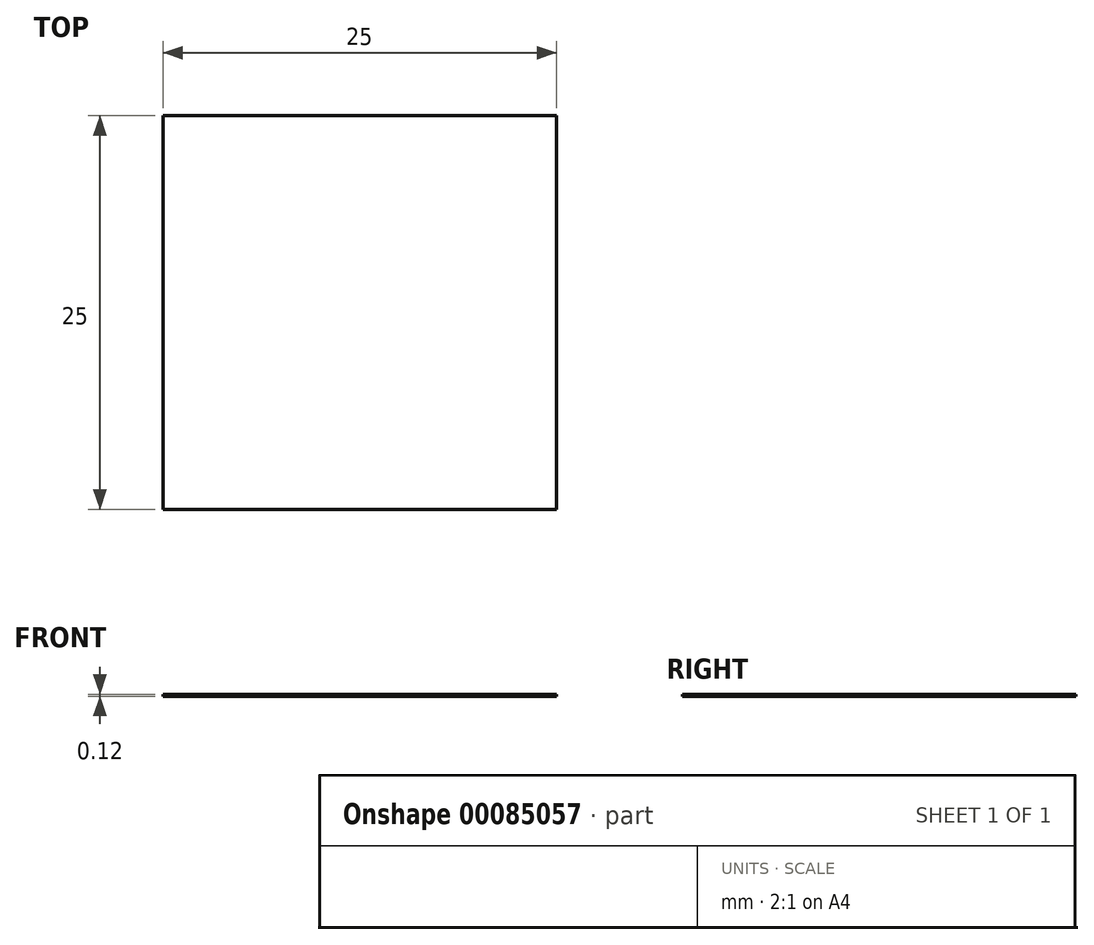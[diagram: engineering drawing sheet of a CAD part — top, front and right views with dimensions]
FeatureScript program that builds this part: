
annotation { "Feature Type Name" : "Feature", "Feature Type Description" : "" }
export const myFeature = defineFeature(function(context is Context, id is Id, definition is map)
    precondition{}
    {
        {
            var Q0;
            Q0=qCreatedBy(makeId("Top.planeOp"),FACE);
            var sketch = newSketch(context, id + "F0", { "sketchPlane" : qUnion([Q0])});
            skLineSegment(sketch, "E0.bottom", {"start": v(12.5, -12.5) * mm, "end": v(-12.5, -12.5) * mm});
            skLineSegment(sketch, "E0.top", {"start": v(12.5, 12.5) * mm, "end": v(-12.5, 12.5) * mm});
            skLineSegment(sketch, "E0.left", {"start": v(12.5, -12.5) * mm, "end": v(12.5, 12.5) * mm});
            skLineSegment(sketch, "E0.right", {"start": v(-12.5, -12.5) * mm, "end": v(-12.5, 12.5) * mm});
            skPoint(sketch, "E0.middle", {"position": v(0, 0) * mm});
            skSolve(sketch);
        }
        {
            var Q0;
            Q0 = qSketchRegion(id + "F0", true);
            extrude(context, id + "F1", {"entities" : qUnion([Q0]), "depth" : .117 * mm});
        }
    });
